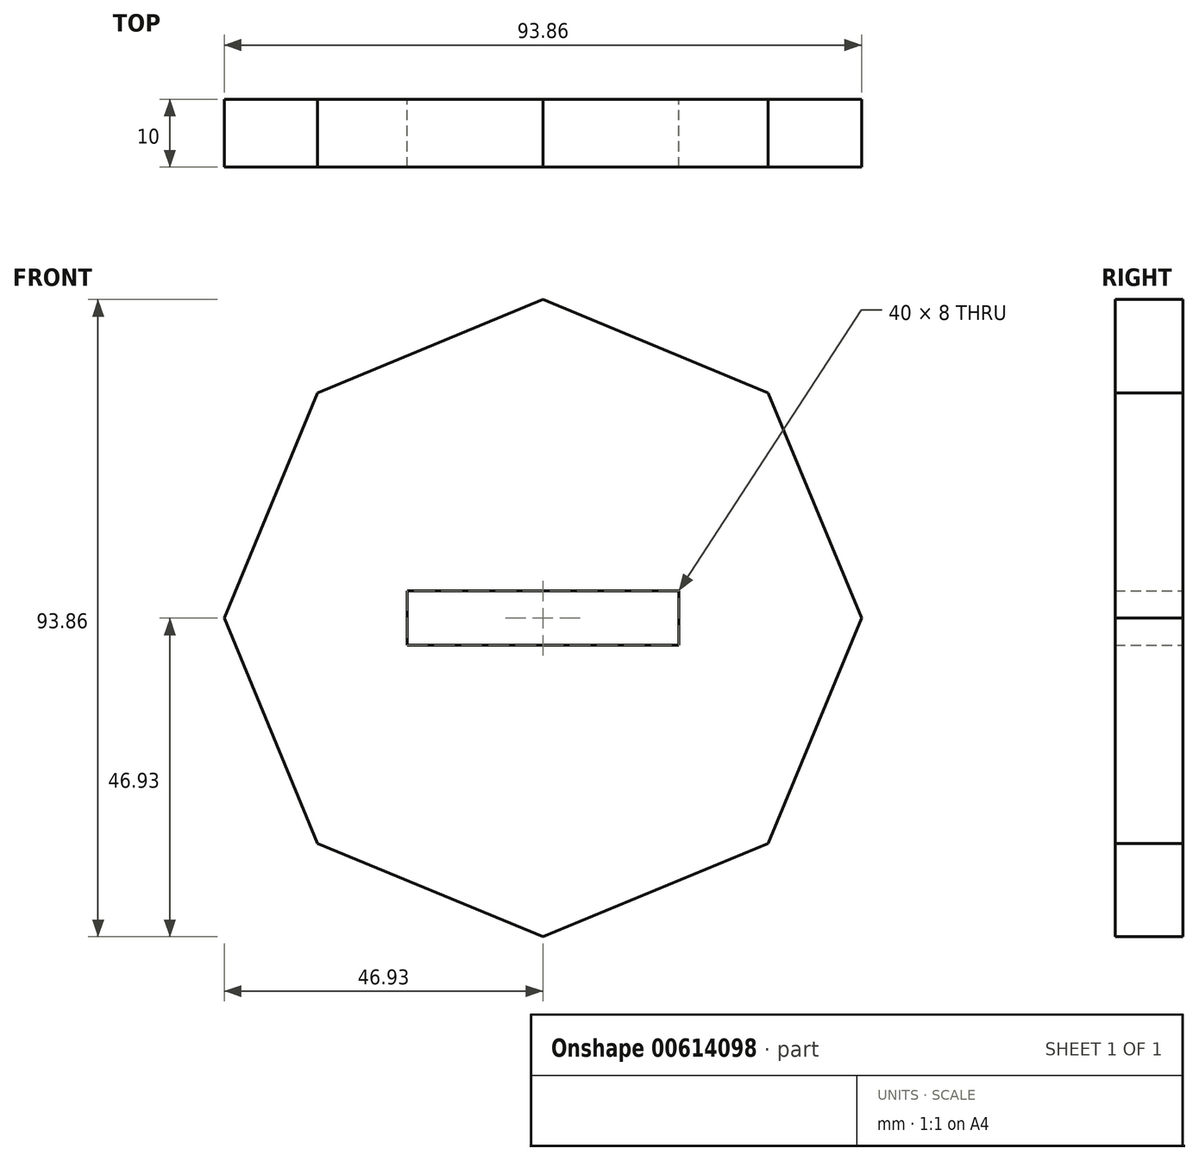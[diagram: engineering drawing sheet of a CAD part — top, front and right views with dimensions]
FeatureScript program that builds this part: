
annotation { "Feature Type Name" : "Feature", "Feature Type Description" : "" }
export const myFeature = defineFeature(function(context is Context, id is Id, definition is map)
    precondition{}
    {
        {
            var Q0;
            Q0=qCreatedBy(makeId("Front.planeOp"),FACE);
            var sketch = newSketch(context, id + "F0", { "sketchPlane" : qUnion([Q0])});
            skCircle(sketch, "E0.cCircle", {"center": v(0, 0) * mm, "radius": 46.93 * mm, "construction": true});
            skLineSegment(sketch, "E0.0", {"start": v(-46.93, 0) * mm, "end": v(-33.19, 33.19) * mm});
            skLineSegment(sketch, "E0.1", {"start": v(-33.19, 33.19) * mm, "end": v(0, 46.93) * mm});
            skLineSegment(sketch, "E0.2", {"start": v(0, 46.93) * mm, "end": v(33.19, 33.19) * mm});
            skLineSegment(sketch, "E0.3", {"start": v(33.19, 33.19) * mm, "end": v(46.93, 0) * mm});
            skLineSegment(sketch, "E0.4", {"start": v(46.93, 0) * mm, "end": v(33.19, -33.19) * mm});
            skLineSegment(sketch, "E0.5", {"start": v(33.19, -33.19) * mm, "end": v(0, -46.93) * mm});
            skLineSegment(sketch, "E0.6", {"start": v(0, -46.93) * mm, "end": v(-33.19, -33.19) * mm});
            skLineSegment(sketch, "E0.7", {"start": v(-33.19, -33.19) * mm, "end": v(-46.93, 0) * mm});
            skLineSegment(sketch, "E1.bottom", {"start": v(0, 0) * mm, "end": v(-20, 0) * mm});
            skLineSegment(sketch, "E1.top", {"start": v(0, 4) * mm, "end": v(-20, 4) * mm});
            skLineSegment(sketch, "E1.left", {"start": v(0, 0) * mm, "end": v(0, 4) * mm});
            skLineSegment(sketch, "E1.right", {"start": v(-20, 0) * mm, "end": v(-20, 4) * mm});
            skLineSegment(sketch, "E2.bottom", {"start": v(0, 0) * mm, "end": v(20, 0) * mm});
            skLineSegment(sketch, "E2.top", {"start": v(0, 4) * mm, "end": v(20, 4) * mm});
            skLineSegment(sketch, "E2.right", {"start": v(20, 0) * mm, "end": v(20, 4) * mm});
            skLineSegment(sketch, "E3.top", {"start": v(0, -4) * mm, "end": v(20, -4) * mm});
            skLineSegment(sketch, "E3.left", {"start": v(0, 0) * mm, "end": v(0, -4) * mm});
            skLineSegment(sketch, "E3.right", {"start": v(20, 0) * mm, "end": v(20, -4) * mm});
            skLineSegment(sketch, "E4.top", {"start": v(0, -4) * mm, "end": v(-20, -4) * mm});
            skLineSegment(sketch, "E4.right", {"start": v(-20, 0) * mm, "end": v(-20, -4) * mm});
            skSolve(sketch);
        }
        {
            var Q0;
            Q0=makeQuery(id+"F0.imprint","IMPRINT",FACE,{"disambiguationData":[TD([[makeQuery(id+"F0.imprint","IMPRINT",EDGE,{"derivedFrom":sQuery(id+"F0.wireOp",EDGE,"E0.0")}),-1.0]])]});
            extrude(context, id + "F1", {"entities" : qUnion([Q0]), "depth" : 10 * mm, "offsetDistance" : 25 * mm});
        }
    });
